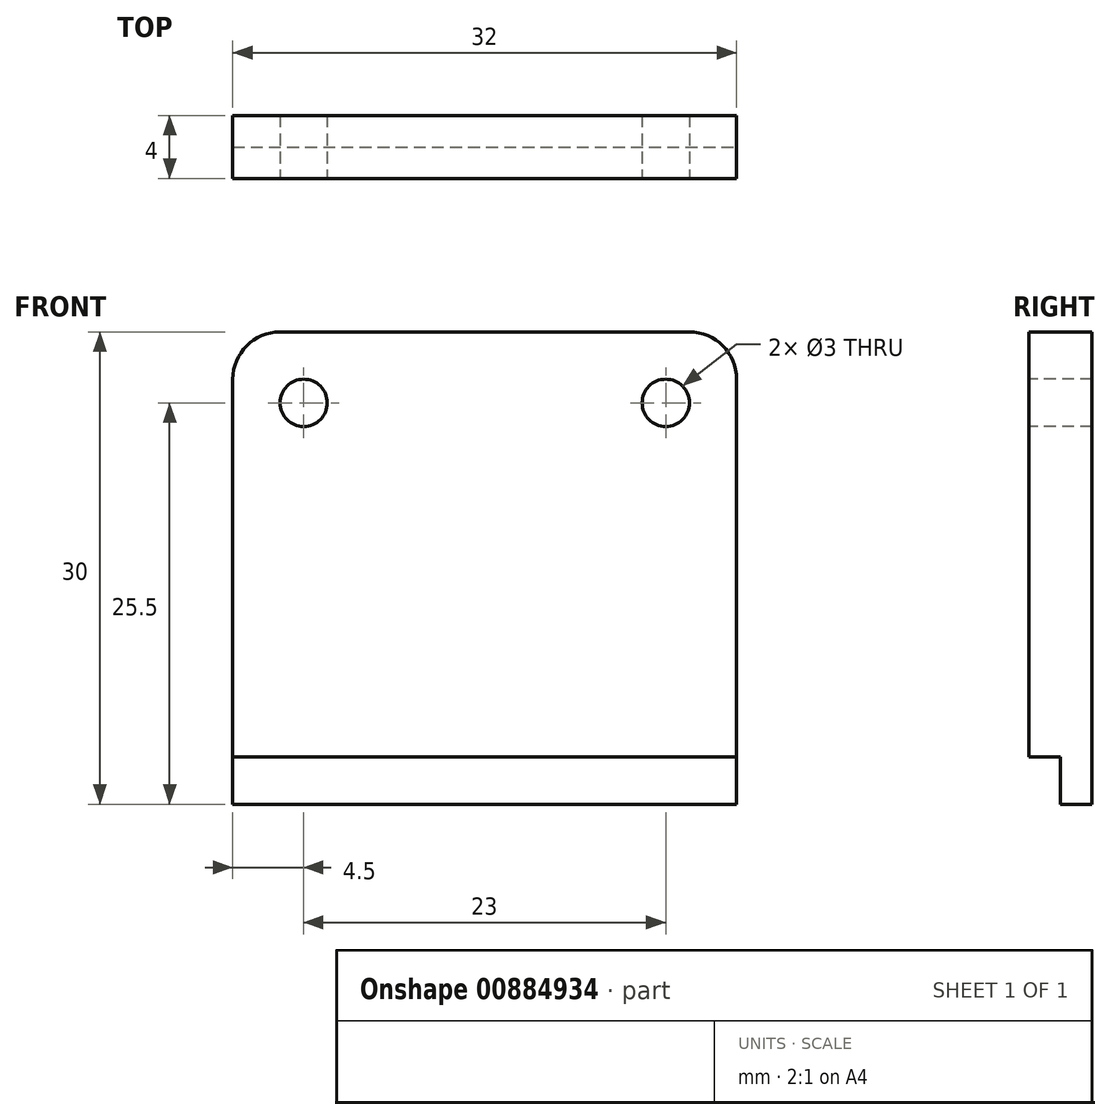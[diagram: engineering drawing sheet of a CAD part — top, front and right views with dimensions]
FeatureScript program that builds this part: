
annotation { "Feature Type Name" : "Feature", "Feature Type Description" : "" }
export const myFeature = defineFeature(function(context is Context, id is Id, definition is map)
    precondition{}
    {
        {
            var Q0;
            Q0=qCreatedBy(makeId("Front.planeOp"),FACE);
            var sketch = newSketch(context, id + "F0", { "sketchPlane" : qUnion([Q0])});
            skLineSegment(sketch, "E0.bottom", {"start": v(-16, 15) * mm, "end": v(16, 15) * mm});
            skLineSegment(sketch, "E0.top", {"start": v(-16, -15) * mm, "end": v(16, -15) * mm});
            skLineSegment(sketch, "E0.left", {"start": v(-16, 15) * mm, "end": v(-16, -15) * mm});
            skLineSegment(sketch, "E0.right", {"start": v(16, 15) * mm, "end": v(16, -15) * mm});
            skPoint(sketch, "E0.middle", {"position": v(0, 0) * mm});
            skSolve(sketch);
        }
        {
            var Q0;
            Q0=makeQuery(id+"F0.imprint","IMPRINT",FACE,{"disambiguationData":[TD([[makeQuery(id+"F0.imprint","IMPRINT",EDGE,{"derivedFrom":sQuery(id+"F0.wireOp",EDGE,"E0.bottom")}),-1.0]])]});
            extrude(context, id + "F1", {"entities" : qUnion([Q0]), "oppositeDirection" : true, "depth" : 2 * mm, "offsetDistance" : 25 * mm});
        }
        {
            var Q0;
            Q0=makeQuery(id+"F1.opExtrude","CAP_FACE",FACE,{"disambiguationData":[OSD([sQuery(id+"F0.wireOp",EDGE,"E0.bottom"),sQuery(id+"F0.wireOp",EDGE,"E0.top"),sQuery(id+"F0.wireOp",EDGE,"E0.left"),sQuery(id+"F0.wireOp",EDGE,"E0.right")])],"isStart":true});
            var sketch = newSketch(context, id + "F2", { "sketchPlane" : qUnion([Q0])});
            skLineSegment(sketch, "E1.0.0", {"start": v(-16, 15) * mm, "end": v(-16, -12) * mm});
            skLineSegment(sketch, "E1.0.2", {"start": v(16, -12) * mm, "end": v(16, 15) * mm});
            skLineSegment(sketch, "E1.0.3", {"start": v(16, 15) * mm, "end": v(-16, 15) * mm});
            skLineSegment(sketch, "E2", {"start": v(-16, -12) * mm, "end": v(16, -12) * mm});
            skPoint(sketch, "E3.orphan", {"position": v(-16, -15) * mm});
            skPoint(sketch, "E4.orphan", {"position": v(16, -15) * mm});
            skSolve(sketch);
        }
        {
            var Q0;
            Q0 = qSketchRegion(id + "F2", true);
            extrude(context, id + "F3", {"entities" : qUnion([Q0]), "operationType" : NewBodyOperationType.ADD, "depth" : 2 * mm, "offsetDistance" : 25 * mm});
        }
        {
            var Q0;
            Q0=makeQuery(id+"F3.opExtrude","CAP_FACE",FACE,{"disambiguationData":[OSD([sQuery(id+"F2.wireOp",EDGE,"E1.0.0"),sQuery(id+"F2.wireOp",EDGE,"E1.0.2"),sQuery(id+"F2.wireOp",EDGE,"E1.0.3"),sQuery(id+"F2.wireOp",EDGE,"E2")])],"isStart":false});
            var sketch = newSketch(context, id + "F4", { "sketchPlane" : qUnion([Q0])});
            skCircle(sketch, "E5", {"center": v(-11.5, 10.5) * mm, "radius": 1.5 * mm});
            skCircle(sketch, "E6.1.0.0", {"center": v(11.5, 10.5) * mm, "radius": 1.5 * mm});
            skLineSegment(sketch, "E6.direction1", {"start": v(-11.5, 10.5) * mm, "end": v(11.5, 10.5) * mm, "construction": true});
            skSolve(sketch);
        }
        {
            var Q0;
            Q0 = qSketchRegion(id + "F4", true);
            extrude(context, id + "F5", {"entities" : qUnion([Q0]), "operationType" : NewBodyOperationType.REMOVE, "endBound" : BoundingType.THROUGH_ALL, "oppositeDirection" : true, "depth" : 25 * mm, "offsetDistance" : 25 * mm});
        }
        {
            var Q0;
            Q0=makeQuery(id+"F3.boolean.opBoolean","MERGE",EDGE,{"derivedFrom":[makeQuery(id+"F1.opExtrude","SWEPT_EDGE",EDGE,{"disambiguationData":[OSD([sQuery(id+"F0.wireOp",EDGE,"E0.bottom"),sQuery(id+"F0.wireOp",EDGE,"E0.left")])]}),makeQuery(id+"F3.opExtrude","SWEPT_EDGE",EDGE,{"disambiguationData":[OSD([sQuery(id+"F2.wireOp",EDGE,"E1.0.0"),sQuery(id+"F2.wireOp",EDGE,"E1.0.3")])]})]});
            var Q1;
            Q1=makeQuery(id+"F3.boolean.opBoolean","MERGE",EDGE,{"derivedFrom":[makeQuery(id+"F1.opExtrude","SWEPT_EDGE",EDGE,{"disambiguationData":[OSD([sQuery(id+"F0.wireOp",EDGE,"E0.bottom"),sQuery(id+"F0.wireOp",EDGE,"E0.right")])]}),makeQuery(id+"F3.opExtrude","SWEPT_EDGE",EDGE,{"disambiguationData":[OSD([sQuery(id+"F2.wireOp",EDGE,"E1.0.2"),sQuery(id+"F2.wireOp",EDGE,"E1.0.3")])]})]});
            fillet(context, id + "F6", {"entities" : qUnion([Q0, Q1]), "radius" : 3 * mm, "tangentPropagation" : true, "allowEdgeOverflow" : false});
        }
    });
